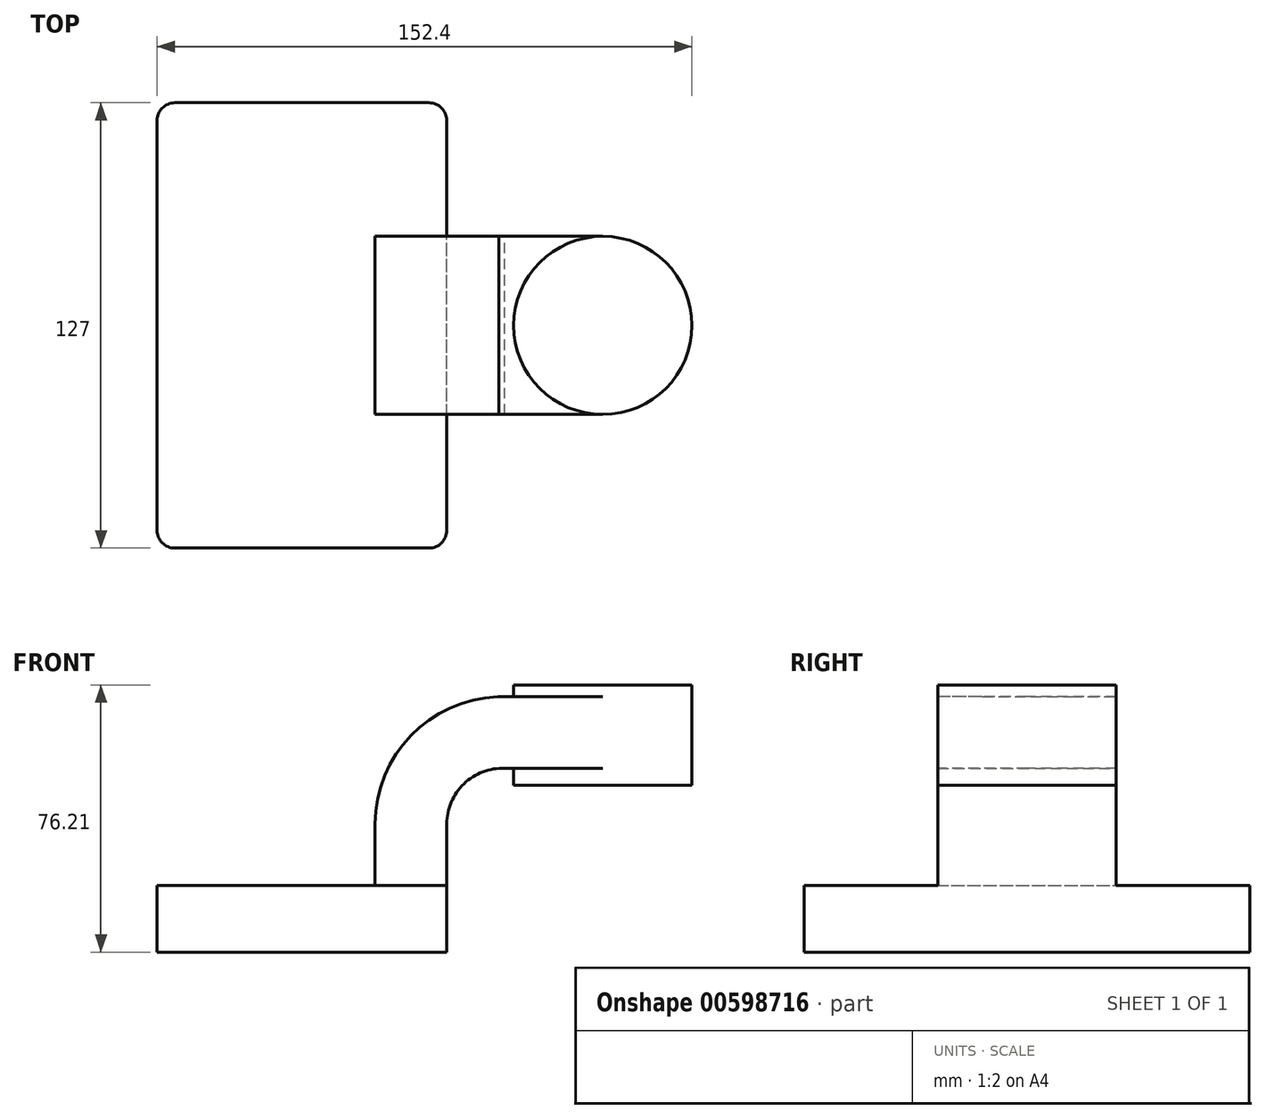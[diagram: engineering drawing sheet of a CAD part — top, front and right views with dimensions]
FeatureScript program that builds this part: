
annotation { "Feature Type Name" : "Feature", "Feature Type Description" : "" }
export const myFeature = defineFeature(function(context is Context, id is Id, definition is map)
    precondition{}
    {
        {
            var Q0;
            Q0=qCreatedBy(makeId("Front.planeOp"),FACE);
            var sketch = newSketch(context, id + "F0", { "sketchPlane" : qUnion([Q0])});
            skLineSegment(sketch, "E0.bottom", {"start": v(41.27, 9.53) * mm, "end": v(-41.28, 9.53) * mm});
            skLineSegment(sketch, "E0.top", {"start": v(41.28, -9.52) * mm, "end": v(-41.27, -9.52) * mm});
            skLineSegment(sketch, "E0.left", {"start": v(41.28, 9.53) * mm, "end": v(41.28, -9.52) * mm});
            skLineSegment(sketch, "E0.right", {"start": v(-41.28, 9.53) * mm, "end": v(-41.27, -9.52) * mm});
            skPoint(sketch, "E0.middle", {"position": v(0, 0) * mm});
            skLineSegment(sketch, "E1", {"start": v(41.27, 9.53) * mm, "end": v(41.27, 27.01) * mm});
            skArc(sketch, "E2", {"start": v(41.28, 27.01) * mm, "mid": v(46.16, 38.47) * mm, "end": v(57.81, 42.88) * mm});
            skLineSegment(sketch, "E3", {"start": v(57.81, 42.88) * mm, "end": v(85.73, 42.88) * mm});
            skLineSegment(sketch, "E4.bottom", {"start": v(111.12, 38.1) * mm, "end": v(60.32, 38.1) * mm});
            skLineSegment(sketch, "E4.top", {"start": v(111.12, 66.68) * mm, "end": v(60.32, 66.68) * mm});
            skLineSegment(sketch, "E4.left", {"start": v(111.12, 38.1) * mm, "end": v(111.12, 66.68) * mm});
            skLineSegment(sketch, "E4.right", {"start": v(60.33, 38.1) * mm, "end": v(60.32, 66.68) * mm});
            skPoint(sketch, "E4.middle", {"position": v(85.72, 52.39) * mm});
            skLineSegment(sketch, "E5.0", {"start": v(56.15, 63.29) * mm, "end": v(85.73, 63.29) * mm});
            skArc(sketch, "E5.1", {"start": v(20.86, 27.01) * mm, "mid": v(31.14, 52.32) * mm, "end": v(56.15, 63.29) * mm});
            skLineSegment(sketch, "E5.2", {"start": v(20.86, 9.53) * mm, "end": v(20.86, 27.01) * mm});
            skLineSegment(sketch, "E6", {"start": v(85.73, 42.88) * mm, "end": v(85.72, 52.39) * mm});
            skLineSegment(sketch, "E7", {"start": v(85.72, 63.29) * mm, "end": v(85.72, 52.39) * mm});
            skLineSegment(sketch, "E8", {"start": v(85.73, 42.88) * mm, "end": v(85.72, 66.68) * mm});
            skLineSegment(sketch, "E9", {"start": v(85.72, 66.68) * mm, "end": v(85.73, 42.88) * mm});
            skLineSegment(sketch, "E10", {"start": v(85.72, 42.88) * mm, "end": v(85.72, 38.1) * mm});
            skFitSpline(sketch, "E11", {"points": [v(-41.28, 9.53) * mm, v(56.15, 63.29) * mm], "startDerivative": vector(47.24, 122.88) * mm, "endDerivative": vector(125.96, 3.93) * mm});
            skSolve(sketch);
        }
        {
            var Q0;
            Q0=makeQuery(id+"F0.imprint","IMPRINT",FACE,{"disambiguationData":[TD([[makeQuery(id+"F0.imprint","IMPRINT",EDGE,{"derivedFrom":sQuery(id+"F0.wireOp",EDGE,"E0.top")}),-1.0]])]});
            extrude(context, id + "F1", {"entities" : qUnion([Q0]), "endBound" : BoundingType.SYMMETRIC, "depth" : 127 * mm, "offsetDistance" : 25.4 * mm});
        }
        {
            var Q0;
            {var subQ8=sQuery(id+"F0.wireOp",EDGE,"E1");Q0=makeQuery(id+"F0.imprint","IMPRINT",FACE,{"disambiguationData":[TD([[makeQuery(id+"F0.imprint","IMPRINT",EDGE,{"derivedFrom":subQ8}),1.0]])]});}
            var Q1;
            {var subQ1=sQuery(id+"F0.wireOp",EDGE,"E3");var subQ3=sQuery(id+"F0.wireOp",EDGE,"E4.right");var subQ4=makeQuery(id+"F0.imprint","INTERSECT",VERTEX,{"derivedFrom":[subQ1,subQ3]});Q1=makeQuery(id+"F0.imprint","IMPRINT",FACE,{"disambiguationData":[TD([[makeQuery(id+"F0.imprint","IMPRINT",EDGE,{"disambiguationData":[TD([[subQ4,-1.0]])],"derivedFrom":subQ3}),-1.0]])]});}
            extrude(context, id + "F2", {"entities" : qUnion([Q0, Q1]), "operationType" : NewBodyOperationType.ADD, "endBound" : BoundingType.SYMMETRIC, "depth" : 50.8 * mm, "offsetDistance" : 25.4 * mm});
        }
        {
            var Q0;
            {var subQ4=sQuery(id+"F0.wireOp",EDGE,"E5.1");Q0=makeQuery(id+"F0.imprint","IMPRINT",FACE,{"disambiguationData":[TD([[makeQuery(id+"F0.imprint","IMPRINT",EDGE,{"derivedFrom":subQ4}),1.0]])]});}
            extrude(context, id + "F3", {"entities" : qUnion([Q0]), "operationType" : NewBodyOperationType.ADD, "endBound" : BoundingType.SYMMETRIC, "depth" : 25.4 * mm, "offsetDistance" : 25.4 * mm});
        }
        {
            var Q0;
            {var subQ0=sQuery(id+"F0.wireOp",EDGE,"E4.left");Q0=makeQuery(id+"F0.imprint","IMPRINT",FACE,{"disambiguationData":[TD([[makeQuery(id+"F0.imprint","IMPRINT",EDGE,{"derivedFrom":subQ0}),1.0]])]});}
            var Q1;
            Q1=sQuery(id+"F0.wireOp",EDGE,"E8");
            revolve(context, id + "F4", {"operationType" : NewBodyOperationType.ADD, "entities" : qUnion([Q0]), "axis" : qUnion([Q1]), "revolveType" : RevolveType.FULL});
        }
        {
            var Q0;
            Q0=makeQuery(id+"F1.opExtrude","CAP_EDGE",EDGE,{"disambiguationData":[OSD([sQuery(id+"F0.wireOp",EDGE,"E0.left")])],"isStart":false});
            var Q1;
            Q1=makeQuery(id+"F1.opExtrude","CAP_EDGE",EDGE,{"disambiguationData":[OSD([sQuery(id+"F0.wireOp",EDGE,"E0.right")])],"isStart":false});
            var Q2;
            Q2=makeQuery(id+"F1.opExtrude","CAP_EDGE",EDGE,{"disambiguationData":[OSD([sQuery(id+"F0.wireOp",EDGE,"E0.right")])],"isStart":true});
            var Q3;
            Q3=makeQuery(id+"F1.opExtrude","CAP_EDGE",EDGE,{"disambiguationData":[OSD([sQuery(id+"F0.wireOp",EDGE,"E0.left")])],"isStart":true});
            fillet(context, id + "F5", {"entities" : qUnion([Q0, Q1, Q2, Q3]), "radius" : 5.08 * mm, "tangentPropagation" : true, "allowEdgeOverflow" : false});
        }
    });
